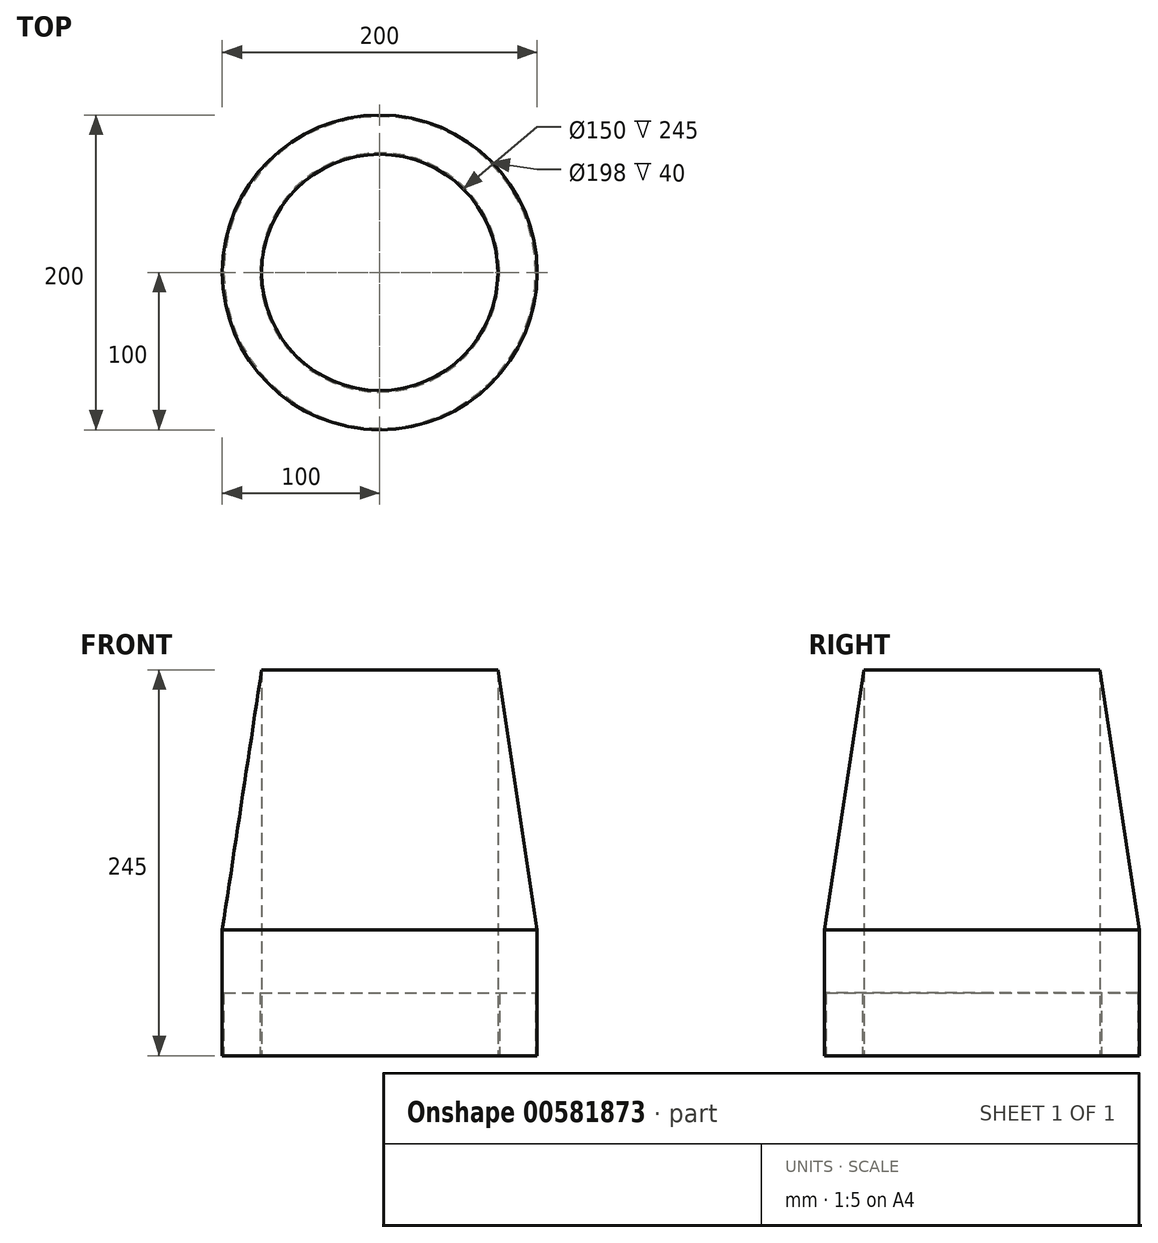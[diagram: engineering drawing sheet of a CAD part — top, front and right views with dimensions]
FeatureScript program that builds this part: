
annotation { "Feature Type Name" : "Feature", "Feature Type Description" : "" }
export const myFeature = defineFeature(function(context is Context, id is Id, definition is map)
    precondition{}
    {
        {
            var Q0;
            Q0=qCreatedBy(makeId("Front.planeOp"),FACE);
            var sketch = newSketch(context, id + "F0", { "sketchPlane" : qUnion([Q0])});
            skLineSegment(sketch, "E0", {"start": v(0, -139.25) * mm, "end": v(0, 240.83) * mm, "construction": true});
            skLineSegment(sketch, "E1", {"start": v(-75, -67.22) * mm, "end": v(-75, 177.78) * mm});
            skLineSegment(sketch, "E2", {"start": v(-75, 177.78) * mm, "end": v(-100, 12.78) * mm});
            skLineSegment(sketch, "E3", {"start": v(-100, 12.78) * mm, "end": v(-100, -67.22) * mm});
            skLineSegment(sketch, "E4", {"start": v(-100, -67.22) * mm, "end": v(-99, -67.22) * mm});
            skLineSegment(sketch, "E5", {"start": v(-99, -67.22) * mm, "end": v(-99, -27.22) * mm});
            skLineSegment(sketch, "E6", {"start": v(-99, -27.22) * mm, "end": v(-76, -27.22) * mm});
            skLineSegment(sketch, "E7", {"start": v(-76, -27.22) * mm, "end": v(-76, -67.22) * mm});
            skLineSegment(sketch, "E8", {"start": v(-76, -67.22) * mm, "end": v(-75, -67.22) * mm});
            skSolve(sketch);
        }
        {
            var Q0;
            Q0=qSketchRegion(id+"F0",true);
            var Q1;
            Q1=sQuery(id+"F0.wireOp",EDGE,"E0");
            revolve(context, id + "F1", {"entities" : qUnion([Q0]), "axis" : qUnion([Q1]), "revolveType" : RevolveType.FULL});
        }
    });
